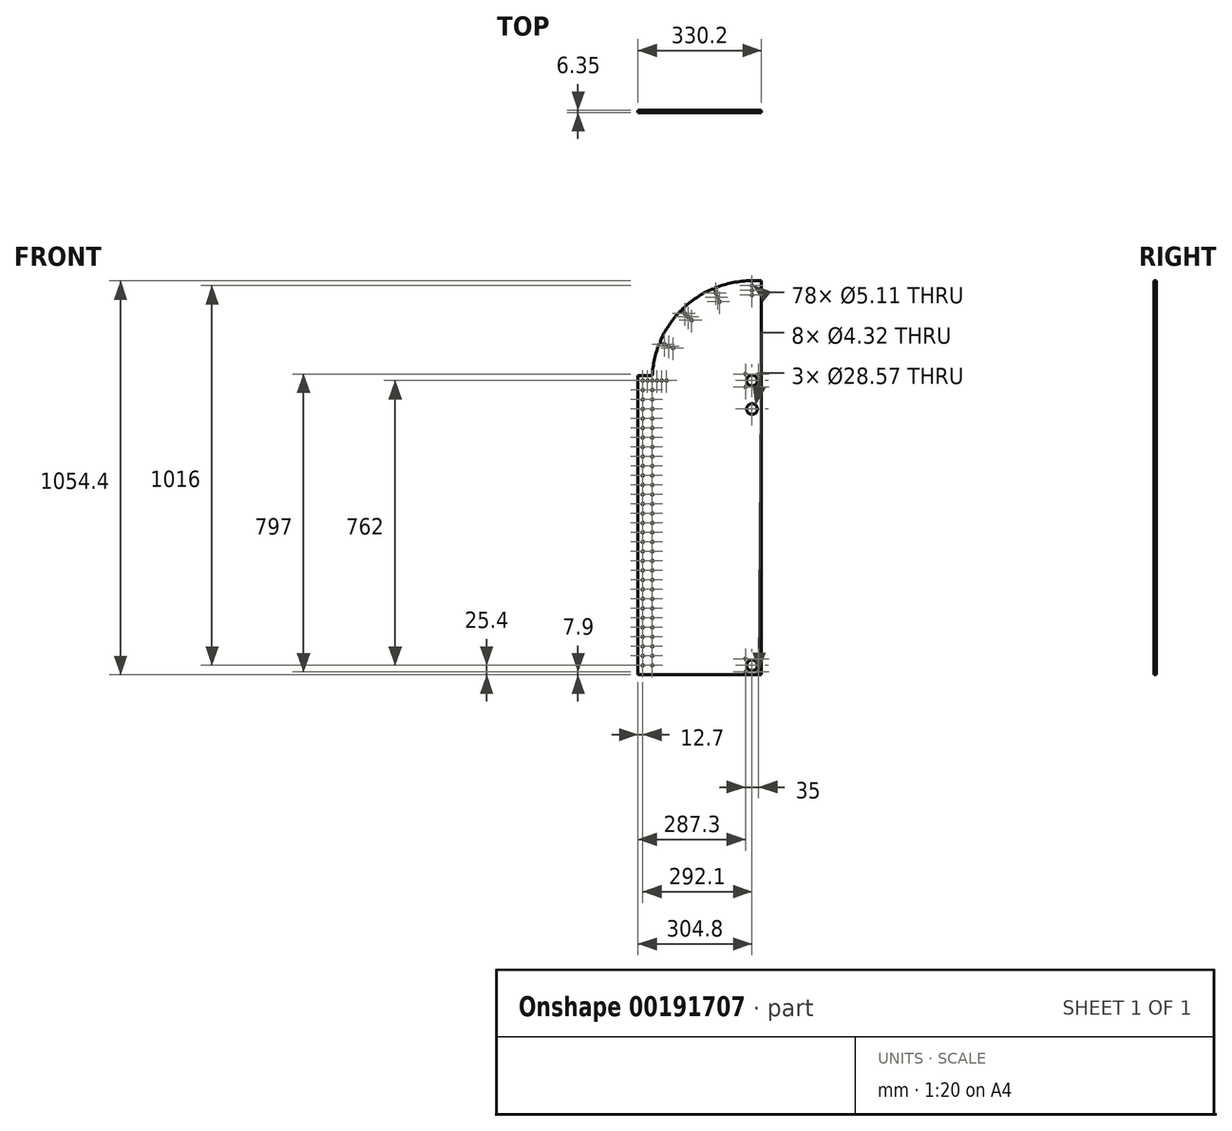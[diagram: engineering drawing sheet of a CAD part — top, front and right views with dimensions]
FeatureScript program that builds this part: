
annotation { "Feature Type Name" : "Feature", "Feature Type Description" : "" }
export const myFeature = defineFeature(function(context is Context, id is Id, definition is map)
    precondition{}
    {
        {
            var Q0;
            Q0=qCreatedBy(makeId("Front.planeOp"),FACE);
            var sketch = newSketch(context, id + "F0", { "sketchPlane" : qUnion([Q0])});
            skCircle(sketch, "E0", {"center": v(0, 0) * mm, "radius": 50.8 * mm, "construction": true});
            skCircle(sketch, "E1", {"center": v(0, 0) * mm, "radius": 14.29 * mm});
            skLineSegment(sketch, "E2", {"start": v(25.4, 0) * mm, "end": v(25.4, -787.4) * mm});
            skCircle(sketch, "E3", {"center": v(0, -76.2) * mm, "radius": 14.29 * mm});
            skLineSegment(sketch, "E4", {"start": v(0, 0) * mm, "end": v(0, -787.4) * mm, "construction": true});
            skCircle(sketch, "E5", {"center": v(0, -76.2) * mm, "radius": 19.05 * mm, "construction": true});
            skCircle(sketch, "E6", {"center": v(0, -762) * mm, "radius": 14.29 * mm});
            skLineSegment(sketch, "E7", {"start": v(25.4, -787.4) * mm, "end": v(-304.8, -787.4) * mm});
            skLineSegment(sketch, "E8", {"start": v(-304.8, -787.4) * mm, "end": v(-304.8, 0) * mm});
            skLineSegment(sketch, "E9", {"start": v(-304.8, 0) * mm, "end": v(-304.8, 304.8) * mm});
            skLineSegment(sketch, "E10", {"start": v(-304.8, 304.8) * mm, "end": v(25.4, 304.8) * mm});
            skLineSegment(sketch, "E11", {"start": v(25.4, 304.8) * mm, "end": v(25.4, 0) * mm});
            skSolve(sketch);
        }
        {
            var Q0;
            Q0 = qSketchRegion(id + "F0", true);
            extrude(context, id + "F1", {"entities" : qUnion([Q0]), "depth" : 6.35 * mm});
        }
        {
            var Q0;
            Q0=makeQuery(id+"F1.opExtrude","CAP_FACE",FACE,{"disambiguationData":[OSD([sQuery(id+"F0.wireOp",EDGE,"E1"),sQuery(id+"F0.wireOp",EDGE,"E2"),sQuery(id+"F0.wireOp",EDGE,"E3"),sQuery(id+"F0.wireOp",EDGE,"E6"),sQuery(id+"F0.wireOp",EDGE,"E7"),sQuery(id+"F0.wireOp",EDGE,"E8"),sQuery(id+"F0.wireOp",EDGE,"E9"),sQuery(id+"F0.wireOp",EDGE,"E10"),sQuery(id+"F0.wireOp",EDGE,"E11")])],"isStart":false});
            var sketch = newSketch(context, id + "F2", { "sketchPlane" : qUnion([Q0])});
            skLineSegment(sketch, "E12", {"start": v(25.4, 0) * mm, "end": v(-304.8, 0) * mm, "construction": true});
            skCircle(sketch, "E13", {"center": v(-292.1, 0) * mm, "radius": 2.55 * mm});
            skCircle(sketch, "E14.0.1.0", {"center": v(-292.1, -25.4) * mm, "radius": 2.55 * mm});
            skCircle(sketch, "E14.0.2.0", {"center": v(-292.1, -50.8) * mm, "radius": 2.55 * mm});
            skCircle(sketch, "E14.0.3.0", {"center": v(-292.1, -76.2) * mm, "radius": 2.55 * mm});
            skCircle(sketch, "E14.0.4.0", {"center": v(-292.1, -101.6) * mm, "radius": 2.55 * mm});
            skCircle(sketch, "E14.0.5.0", {"center": v(-292.1, -127) * mm, "radius": 2.55 * mm});
            skCircle(sketch, "E14.0.6.0", {"center": v(-292.1, -152.4) * mm, "radius": 2.55 * mm});
            skCircle(sketch, "E14.0.7.0", {"center": v(-292.1, -177.8) * mm, "radius": 2.55 * mm});
            skCircle(sketch, "E14.0.8.0", {"center": v(-292.1, -203.2) * mm, "radius": 2.55 * mm});
            skCircle(sketch, "E14.0.9.0", {"center": v(-292.1, -228.6) * mm, "radius": 2.55 * mm});
            skCircle(sketch, "E14.0.10.0", {"center": v(-292.1, -254) * mm, "radius": 2.55 * mm});
            skCircle(sketch, "E14.0.11.0", {"center": v(-292.1, -279.4) * mm, "radius": 2.55 * mm});
            skCircle(sketch, "E14.0.12.0", {"center": v(-292.1, -304.8) * mm, "radius": 2.55 * mm});
            skCircle(sketch, "E14.0.13.0", {"center": v(-292.1, -330.2) * mm, "radius": 2.55 * mm});
            skCircle(sketch, "E14.0.14.0", {"center": v(-292.1, -355.6) * mm, "radius": 2.55 * mm});
            skCircle(sketch, "E14.0.15.0", {"center": v(-292.1, -381) * mm, "radius": 2.55 * mm});
            skCircle(sketch, "E14.0.16.0", {"center": v(-292.1, -406.4) * mm, "radius": 2.55 * mm});
            skCircle(sketch, "E14.0.17.0", {"center": v(-292.1, -431.8) * mm, "radius": 2.55 * mm});
            skCircle(sketch, "E14.0.18.0", {"center": v(-292.1, -457.2) * mm, "radius": 2.55 * mm});
            skCircle(sketch, "E14.0.19.0", {"center": v(-292.1, -482.6) * mm, "radius": 2.55 * mm});
            skCircle(sketch, "E14.0.20.0", {"center": v(-292.1, -508) * mm, "radius": 2.55 * mm});
            skCircle(sketch, "E14.0.21.0", {"center": v(-292.1, -533.4) * mm, "radius": 2.55 * mm});
            skCircle(sketch, "E14.0.22.0", {"center": v(-292.1, -558.8) * mm, "radius": 2.55 * mm});
            skCircle(sketch, "E14.0.23.0", {"center": v(-292.1, -584.2) * mm, "radius": 2.55 * mm});
            skCircle(sketch, "E14.0.24.0", {"center": v(-292.1, -609.6) * mm, "radius": 2.55 * mm});
            skCircle(sketch, "E14.0.25.0", {"center": v(-292.1, -635) * mm, "radius": 2.55 * mm});
            skCircle(sketch, "E14.0.26.0", {"center": v(-292.1, -660.4) * mm, "radius": 2.55 * mm});
            skCircle(sketch, "E14.0.27.0", {"center": v(-292.1, -685.8) * mm, "radius": 2.55 * mm});
            skCircle(sketch, "E14.0.28.0", {"center": v(-292.1, -711.2) * mm, "radius": 2.55 * mm});
            skCircle(sketch, "E14.0.29.0", {"center": v(-292.1, -736.6) * mm, "radius": 2.55 * mm});
            skCircle(sketch, "E14.0.30.0", {"center": v(-292.1, -762) * mm, "radius": 2.55 * mm});
            skCircle(sketch, "E14.1.0.0", {"center": v(-266.7, 0) * mm, "radius": 2.55 * mm});
            skCircle(sketch, "E14.1.1.0", {"center": v(-266.7, -25.4) * mm, "radius": 2.55 * mm});
            skCircle(sketch, "E14.1.2.0", {"center": v(-266.7, -50.8) * mm, "radius": 2.55 * mm});
            skCircle(sketch, "E14.1.3.0", {"center": v(-266.7, -76.2) * mm, "radius": 2.55 * mm});
            skCircle(sketch, "E14.1.4.0", {"center": v(-266.7, -101.6) * mm, "radius": 2.55 * mm});
            skCircle(sketch, "E14.1.5.0", {"center": v(-266.7, -127) * mm, "radius": 2.55 * mm});
            skCircle(sketch, "E14.1.6.0", {"center": v(-266.7, -152.4) * mm, "radius": 2.55 * mm});
            skCircle(sketch, "E14.1.7.0", {"center": v(-266.7, -177.8) * mm, "radius": 2.55 * mm});
            skCircle(sketch, "E14.1.8.0", {"center": v(-266.7, -203.2) * mm, "radius": 2.55 * mm});
            skCircle(sketch, "E14.1.9.0", {"center": v(-266.7, -228.6) * mm, "radius": 2.55 * mm});
            skCircle(sketch, "E14.1.10.0", {"center": v(-266.7, -254) * mm, "radius": 2.55 * mm});
            skCircle(sketch, "E14.1.11.0", {"center": v(-266.7, -279.4) * mm, "radius": 2.55 * mm});
            skCircle(sketch, "E14.1.12.0", {"center": v(-266.7, -304.8) * mm, "radius": 2.55 * mm});
            skCircle(sketch, "E14.1.13.0", {"center": v(-266.7, -330.2) * mm, "radius": 2.55 * mm});
            skCircle(sketch, "E14.1.14.0", {"center": v(-266.7, -355.6) * mm, "radius": 2.55 * mm});
            skCircle(sketch, "E14.1.15.0", {"center": v(-266.7, -381) * mm, "radius": 2.55 * mm});
            skCircle(sketch, "E14.1.16.0", {"center": v(-266.7, -406.4) * mm, "radius": 2.55 * mm});
            skCircle(sketch, "E14.1.17.0", {"center": v(-266.7, -431.8) * mm, "radius": 2.55 * mm});
            skCircle(sketch, "E14.1.18.0", {"center": v(-266.7, -457.2) * mm, "radius": 2.55 * mm});
            skCircle(sketch, "E14.1.19.0", {"center": v(-266.7, -482.6) * mm, "radius": 2.55 * mm});
            skCircle(sketch, "E14.1.20.0", {"center": v(-266.7, -508) * mm, "radius": 2.55 * mm});
            skCircle(sketch, "E14.1.21.0", {"center": v(-266.7, -533.4) * mm, "radius": 2.55 * mm});
            skCircle(sketch, "E14.1.22.0", {"center": v(-266.7, -558.8) * mm, "radius": 2.55 * mm});
            skCircle(sketch, "E14.1.23.0", {"center": v(-266.7, -584.2) * mm, "radius": 2.55 * mm});
            skCircle(sketch, "E14.1.24.0", {"center": v(-266.7, -609.6) * mm, "radius": 2.55 * mm});
            skCircle(sketch, "E14.1.25.0", {"center": v(-266.7, -635) * mm, "radius": 2.55 * mm});
            skCircle(sketch, "E14.1.26.0", {"center": v(-266.7, -660.4) * mm, "radius": 2.55 * mm});
            skCircle(sketch, "E14.1.27.0", {"center": v(-266.7, -685.8) * mm, "radius": 2.55 * mm});
            skCircle(sketch, "E14.1.28.0", {"center": v(-266.7, -711.2) * mm, "radius": 2.55 * mm});
            skCircle(sketch, "E14.1.29.0", {"center": v(-266.7, -736.6) * mm, "radius": 2.55 * mm});
            skCircle(sketch, "E14.1.30.0", {"center": v(-266.7, -762) * mm, "radius": 2.55 * mm});
            skLineSegment(sketch, "E14.direction1", {"start": v(-292.1, 0) * mm, "end": v(-266.7, 0) * mm, "construction": true});
            skLineSegment(sketch, "E14.direction2", {"start": v(-292.1, 0) * mm, "end": v(-292.1, -25.4) * mm, "construction": true});
            skSolve(sketch);
        }
        {
            var Q0;
            Q0=makeQuery(id+"F2.imprint","IMPRINT",FACE,{"disambiguationData":[TD([[makeQuery(id+"F2.imprint","IMPRINT",EDGE,{"derivedFrom":sQuery(id+"F2.wireOp",EDGE,"E14.0.1.0")}),1.0]])]});
            var Q1;
            Q1=makeQuery(id+"F2.imprint","IMPRINT",FACE,{"disambiguationData":[TD([[makeQuery(id+"F2.imprint","IMPRINT",EDGE,{"derivedFrom":sQuery(id+"F2.wireOp",EDGE,"E14.0.2.0")}),1.0]])]});
            var Q2;
            Q2=makeQuery(id+"F2.imprint","IMPRINT",FACE,{"disambiguationData":[TD([[makeQuery(id+"F2.imprint","IMPRINT",EDGE,{"derivedFrom":sQuery(id+"F2.wireOp",EDGE,"E14.1.2.0")}),1.0]])]});
            var Q3;
            Q3=makeQuery(id+"F2.imprint","IMPRINT",FACE,{"disambiguationData":[TD([[makeQuery(id+"F2.imprint","IMPRINT",EDGE,{"derivedFrom":sQuery(id+"F2.wireOp",EDGE,"E14.1.1.0")}),1.0]])]});
            var Q4;
            Q4=makeQuery(id+"F2.imprint","IMPRINT",FACE,{"disambiguationData":[TD([[makeQuery(id+"F2.imprint","IMPRINT",EDGE,{"derivedFrom":sQuery(id+"F2.wireOp",EDGE,"E14.1.0.0")}),1.0]])]});
            var Q5;
            Q5=makeQuery(id+"F2.imprint","IMPRINT",FACE,{"disambiguationData":[TD([[makeQuery(id+"F2.imprint","IMPRINT",EDGE,{"derivedFrom":sQuery(id+"F2.wireOp",EDGE,"E13")}),1.0]])]});
            var Q6;
            Q6=makeQuery(id+"F2.imprint","IMPRINT",FACE,{"disambiguationData":[TD([[makeQuery(id+"F2.imprint","IMPRINT",EDGE,{"derivedFrom":sQuery(id+"F2.wireOp",EDGE,"E14.0.3.0")}),1.0]])]});
            var Q7;
            Q7=makeQuery(id+"F2.imprint","IMPRINT",FACE,{"disambiguationData":[TD([[makeQuery(id+"F2.imprint","IMPRINT",EDGE,{"derivedFrom":sQuery(id+"F2.wireOp",EDGE,"E14.1.3.0")}),1.0]])]});
            var Q8;
            Q8=makeQuery(id+"F2.imprint","IMPRINT",FACE,{"disambiguationData":[TD([[makeQuery(id+"F2.imprint","IMPRINT",EDGE,{"derivedFrom":sQuery(id+"F2.wireOp",EDGE,"E14.0.4.0")}),1.0]])]});
            var Q9;
            Q9=makeQuery(id+"F2.imprint","IMPRINT",FACE,{"disambiguationData":[TD([[makeQuery(id+"F2.imprint","IMPRINT",EDGE,{"derivedFrom":sQuery(id+"F2.wireOp",EDGE,"E14.1.4.0")}),1.0]])]});
            var Q10;
            Q10=makeQuery(id+"F2.imprint","IMPRINT",FACE,{"disambiguationData":[TD([[makeQuery(id+"F2.imprint","IMPRINT",EDGE,{"derivedFrom":sQuery(id+"F2.wireOp",EDGE,"E14.1.5.0")}),1.0]])]});
            var Q11;
            Q11=makeQuery(id+"F2.imprint","IMPRINT",FACE,{"disambiguationData":[TD([[makeQuery(id+"F2.imprint","IMPRINT",EDGE,{"derivedFrom":sQuery(id+"F2.wireOp",EDGE,"E14.0.5.0")}),1.0]])]});
            var Q12;
            Q12=makeQuery(id+"F2.imprint","IMPRINT",FACE,{"disambiguationData":[TD([[makeQuery(id+"F2.imprint","IMPRINT",EDGE,{"derivedFrom":sQuery(id+"F2.wireOp",EDGE,"E14.0.6.0")}),1.0]])]});
            var Q13;
            Q13=makeQuery(id+"F2.imprint","IMPRINT",FACE,{"disambiguationData":[TD([[makeQuery(id+"F2.imprint","IMPRINT",EDGE,{"derivedFrom":sQuery(id+"F2.wireOp",EDGE,"E14.1.6.0")}),1.0]])]});
            var Q14;
            Q14=makeQuery(id+"F2.imprint","IMPRINT",FACE,{"disambiguationData":[TD([[makeQuery(id+"F2.imprint","IMPRINT",EDGE,{"derivedFrom":sQuery(id+"F2.wireOp",EDGE,"E14.0.7.0")}),1.0]])]});
            var Q15;
            Q15=makeQuery(id+"F2.imprint","IMPRINT",FACE,{"disambiguationData":[TD([[makeQuery(id+"F2.imprint","IMPRINT",EDGE,{"derivedFrom":sQuery(id+"F2.wireOp",EDGE,"E14.1.7.0")}),1.0]])]});
            var Q16;
            Q16=makeQuery(id+"F2.imprint","IMPRINT",FACE,{"disambiguationData":[TD([[makeQuery(id+"F2.imprint","IMPRINT",EDGE,{"derivedFrom":sQuery(id+"F2.wireOp",EDGE,"E14.1.8.0")}),1.0]])]});
            var Q17;
            Q17=makeQuery(id+"F2.imprint","IMPRINT",FACE,{"disambiguationData":[TD([[makeQuery(id+"F2.imprint","IMPRINT",EDGE,{"derivedFrom":sQuery(id+"F2.wireOp",EDGE,"E14.0.8.0")}),1.0]])]});
            var Q18;
            Q18=makeQuery(id+"F2.imprint","IMPRINT",FACE,{"disambiguationData":[TD([[makeQuery(id+"F2.imprint","IMPRINT",EDGE,{"derivedFrom":sQuery(id+"F2.wireOp",EDGE,"E14.0.9.0")}),1.0]])]});
            var Q19;
            Q19=makeQuery(id+"F2.imprint","IMPRINT",FACE,{"disambiguationData":[TD([[makeQuery(id+"F2.imprint","IMPRINT",EDGE,{"derivedFrom":sQuery(id+"F2.wireOp",EDGE,"E14.1.9.0")}),1.0]])]});
            var Q20;
            Q20=makeQuery(id+"F2.imprint","IMPRINT",FACE,{"disambiguationData":[TD([[makeQuery(id+"F2.imprint","IMPRINT",EDGE,{"derivedFrom":sQuery(id+"F2.wireOp",EDGE,"E14.0.10.0")}),1.0]])]});
            var Q21;
            Q21=makeQuery(id+"F2.imprint","IMPRINT",FACE,{"disambiguationData":[TD([[makeQuery(id+"F2.imprint","IMPRINT",EDGE,{"derivedFrom":sQuery(id+"F2.wireOp",EDGE,"E14.1.10.0")}),1.0]])]});
            var Q22;
            Q22=makeQuery(id+"F2.imprint","IMPRINT",FACE,{"disambiguationData":[TD([[makeQuery(id+"F2.imprint","IMPRINT",EDGE,{"derivedFrom":sQuery(id+"F2.wireOp",EDGE,"E14.1.11.0")}),1.0]])]});
            var Q23;
            Q23=makeQuery(id+"F2.imprint","IMPRINT",FACE,{"disambiguationData":[TD([[makeQuery(id+"F2.imprint","IMPRINT",EDGE,{"derivedFrom":sQuery(id+"F2.wireOp",EDGE,"E14.0.11.0")}),1.0]])]});
            var Q24;
            Q24=makeQuery(id+"F2.imprint","IMPRINT",FACE,{"disambiguationData":[TD([[makeQuery(id+"F2.imprint","IMPRINT",EDGE,{"derivedFrom":sQuery(id+"F2.wireOp",EDGE,"E14.0.12.0")}),1.0]])]});
            var Q25;
            Q25=makeQuery(id+"F2.imprint","IMPRINT",FACE,{"disambiguationData":[TD([[makeQuery(id+"F2.imprint","IMPRINT",EDGE,{"derivedFrom":sQuery(id+"F2.wireOp",EDGE,"E14.1.12.0")}),1.0]])]});
            var Q26;
            Q26=makeQuery(id+"F2.imprint","IMPRINT",FACE,{"disambiguationData":[TD([[makeQuery(id+"F2.imprint","IMPRINT",EDGE,{"derivedFrom":sQuery(id+"F2.wireOp",EDGE,"E14.1.13.0")}),1.0]])]});
            var Q27;
            Q27=makeQuery(id+"F2.imprint","IMPRINT",FACE,{"disambiguationData":[TD([[makeQuery(id+"F2.imprint","IMPRINT",EDGE,{"derivedFrom":sQuery(id+"F2.wireOp",EDGE,"E14.0.13.0")}),1.0]])]});
            var Q28;
            Q28=makeQuery(id+"F2.imprint","IMPRINT",FACE,{"disambiguationData":[TD([[makeQuery(id+"F2.imprint","IMPRINT",EDGE,{"derivedFrom":sQuery(id+"F2.wireOp",EDGE,"E14.0.14.0")}),1.0]])]});
            var Q29;
            Q29=makeQuery(id+"F2.imprint","IMPRINT",FACE,{"disambiguationData":[TD([[makeQuery(id+"F2.imprint","IMPRINT",EDGE,{"derivedFrom":sQuery(id+"F2.wireOp",EDGE,"E14.1.14.0")}),1.0]])]});
            var Q30;
            Q30=makeQuery(id+"F2.imprint","IMPRINT",FACE,{"disambiguationData":[TD([[makeQuery(id+"F2.imprint","IMPRINT",EDGE,{"derivedFrom":sQuery(id+"F2.wireOp",EDGE,"E14.1.15.0")}),1.0]])]});
            var Q31;
            Q31=makeQuery(id+"F2.imprint","IMPRINT",FACE,{"disambiguationData":[TD([[makeQuery(id+"F2.imprint","IMPRINT",EDGE,{"derivedFrom":sQuery(id+"F2.wireOp",EDGE,"E14.0.15.0")}),1.0]])]});
            var Q32;
            Q32=makeQuery(id+"F2.imprint","IMPRINT",FACE,{"disambiguationData":[TD([[makeQuery(id+"F2.imprint","IMPRINT",EDGE,{"derivedFrom":sQuery(id+"F2.wireOp",EDGE,"E14.1.16.0")}),1.0]])]});
            var Q33;
            Q33=makeQuery(id+"F2.imprint","IMPRINT",FACE,{"disambiguationData":[TD([[makeQuery(id+"F2.imprint","IMPRINT",EDGE,{"derivedFrom":sQuery(id+"F2.wireOp",EDGE,"E14.0.16.0")}),1.0]])]});
            var Q34;
            Q34=makeQuery(id+"F2.imprint","IMPRINT",FACE,{"disambiguationData":[TD([[makeQuery(id+"F2.imprint","IMPRINT",EDGE,{"derivedFrom":sQuery(id+"F2.wireOp",EDGE,"E14.0.17.0")}),1.0]])]});
            var Q35;
            Q35=makeQuery(id+"F2.imprint","IMPRINT",FACE,{"disambiguationData":[TD([[makeQuery(id+"F2.imprint","IMPRINT",EDGE,{"derivedFrom":sQuery(id+"F2.wireOp",EDGE,"E14.1.17.0")}),1.0]])]});
            var Q36;
            Q36=makeQuery(id+"F2.imprint","IMPRINT",FACE,{"disambiguationData":[TD([[makeQuery(id+"F2.imprint","IMPRINT",EDGE,{"derivedFrom":sQuery(id+"F2.wireOp",EDGE,"E14.1.18.0")}),1.0]])]});
            var Q37;
            Q37=makeQuery(id+"F2.imprint","IMPRINT",FACE,{"disambiguationData":[TD([[makeQuery(id+"F2.imprint","IMPRINT",EDGE,{"derivedFrom":sQuery(id+"F2.wireOp",EDGE,"E14.0.18.0")}),1.0]])]});
            var Q38;
            Q38=makeQuery(id+"F2.imprint","IMPRINT",FACE,{"disambiguationData":[TD([[makeQuery(id+"F2.imprint","IMPRINT",EDGE,{"derivedFrom":sQuery(id+"F2.wireOp",EDGE,"E14.1.19.0")}),1.0]])]});
            var Q39;
            Q39=makeQuery(id+"F2.imprint","IMPRINT",FACE,{"disambiguationData":[TD([[makeQuery(id+"F2.imprint","IMPRINT",EDGE,{"derivedFrom":sQuery(id+"F2.wireOp",EDGE,"E14.0.19.0")}),1.0]])]});
            var Q40;
            Q40=makeQuery(id+"F2.imprint","IMPRINT",FACE,{"disambiguationData":[TD([[makeQuery(id+"F2.imprint","IMPRINT",EDGE,{"derivedFrom":sQuery(id+"F2.wireOp",EDGE,"E14.0.20.0")}),1.0]])]});
            var Q41;
            Q41=makeQuery(id+"F2.imprint","IMPRINT",FACE,{"disambiguationData":[TD([[makeQuery(id+"F2.imprint","IMPRINT",EDGE,{"derivedFrom":sQuery(id+"F2.wireOp",EDGE,"E14.1.20.0")}),1.0]])]});
            var Q42;
            Q42=makeQuery(id+"F2.imprint","IMPRINT",FACE,{"disambiguationData":[TD([[makeQuery(id+"F2.imprint","IMPRINT",EDGE,{"derivedFrom":sQuery(id+"F2.wireOp",EDGE,"E14.1.21.0")}),1.0]])]});
            var Q43;
            Q43=makeQuery(id+"F2.imprint","IMPRINT",FACE,{"disambiguationData":[TD([[makeQuery(id+"F2.imprint","IMPRINT",EDGE,{"derivedFrom":sQuery(id+"F2.wireOp",EDGE,"E14.0.21.0")}),1.0]])]});
            var Q44;
            Q44=makeQuery(id+"F2.imprint","IMPRINT",FACE,{"disambiguationData":[TD([[makeQuery(id+"F2.imprint","IMPRINT",EDGE,{"derivedFrom":sQuery(id+"F2.wireOp",EDGE,"E14.1.22.0")}),1.0]])]});
            var Q45;
            Q45=makeQuery(id+"F2.imprint","IMPRINT",FACE,{"disambiguationData":[TD([[makeQuery(id+"F2.imprint","IMPRINT",EDGE,{"derivedFrom":sQuery(id+"F2.wireOp",EDGE,"E14.0.22.0")}),1.0]])]});
            var Q46;
            Q46=makeQuery(id+"F2.imprint","IMPRINT",FACE,{"disambiguationData":[TD([[makeQuery(id+"F2.imprint","IMPRINT",EDGE,{"derivedFrom":sQuery(id+"F2.wireOp",EDGE,"E14.0.23.0")}),1.0]])]});
            var Q47;
            Q47=makeQuery(id+"F2.imprint","IMPRINT",FACE,{"disambiguationData":[TD([[makeQuery(id+"F2.imprint","IMPRINT",EDGE,{"derivedFrom":sQuery(id+"F2.wireOp",EDGE,"E14.1.23.0")}),1.0]])]});
            var Q48;
            Q48=makeQuery(id+"F2.imprint","IMPRINT",FACE,{"disambiguationData":[TD([[makeQuery(id+"F2.imprint","IMPRINT",EDGE,{"derivedFrom":sQuery(id+"F2.wireOp",EDGE,"E14.1.24.0")}),1.0]])]});
            var Q49;
            Q49=makeQuery(id+"F2.imprint","IMPRINT",FACE,{"disambiguationData":[TD([[makeQuery(id+"F2.imprint","IMPRINT",EDGE,{"derivedFrom":sQuery(id+"F2.wireOp",EDGE,"E14.0.24.0")}),1.0]])]});
            var Q50;
            Q50=makeQuery(id+"F2.imprint","IMPRINT",FACE,{"disambiguationData":[TD([[makeQuery(id+"F2.imprint","IMPRINT",EDGE,{"derivedFrom":sQuery(id+"F2.wireOp",EDGE,"E14.1.25.0")}),1.0]])]});
            var Q51;
            Q51=makeQuery(id+"F2.imprint","IMPRINT",FACE,{"disambiguationData":[TD([[makeQuery(id+"F2.imprint","IMPRINT",EDGE,{"derivedFrom":sQuery(id+"F2.wireOp",EDGE,"E14.0.25.0")}),1.0]])]});
            var Q52;
            Q52=makeQuery(id+"F2.imprint","IMPRINT",FACE,{"disambiguationData":[TD([[makeQuery(id+"F2.imprint","IMPRINT",EDGE,{"derivedFrom":sQuery(id+"F2.wireOp",EDGE,"E14.0.26.0")}),1.0]])]});
            var Q53;
            Q53=makeQuery(id+"F2.imprint","IMPRINT",FACE,{"disambiguationData":[TD([[makeQuery(id+"F2.imprint","IMPRINT",EDGE,{"derivedFrom":sQuery(id+"F2.wireOp",EDGE,"E14.1.26.0")}),1.0]])]});
            var Q54;
            Q54=makeQuery(id+"F2.imprint","IMPRINT",FACE,{"disambiguationData":[TD([[makeQuery(id+"F2.imprint","IMPRINT",EDGE,{"derivedFrom":sQuery(id+"F2.wireOp",EDGE,"E14.1.27.0")}),1.0]])]});
            var Q55;
            Q55=makeQuery(id+"F2.imprint","IMPRINT",FACE,{"disambiguationData":[TD([[makeQuery(id+"F2.imprint","IMPRINT",EDGE,{"derivedFrom":sQuery(id+"F2.wireOp",EDGE,"E14.0.27.0")}),1.0]])]});
            var Q56;
            Q56=makeQuery(id+"F2.imprint","IMPRINT",FACE,{"disambiguationData":[TD([[makeQuery(id+"F2.imprint","IMPRINT",EDGE,{"derivedFrom":sQuery(id+"F2.wireOp",EDGE,"E14.1.28.0")}),1.0]])]});
            var Q57;
            Q57=makeQuery(id+"F2.imprint","IMPRINT",FACE,{"disambiguationData":[TD([[makeQuery(id+"F2.imprint","IMPRINT",EDGE,{"derivedFrom":sQuery(id+"F2.wireOp",EDGE,"E14.0.28.0")}),1.0]])]});
            var Q58;
            Q58=makeQuery(id+"F2.imprint","IMPRINT",FACE,{"disambiguationData":[TD([[makeQuery(id+"F2.imprint","IMPRINT",EDGE,{"derivedFrom":sQuery(id+"F2.wireOp",EDGE,"E14.0.29.0")}),1.0]])]});
            var Q59;
            Q59=makeQuery(id+"F2.imprint","IMPRINT",FACE,{"disambiguationData":[TD([[makeQuery(id+"F2.imprint","IMPRINT",EDGE,{"derivedFrom":sQuery(id+"F2.wireOp",EDGE,"E14.1.29.0")}),1.0]])]});
            var Q60;
            Q60=makeQuery(id+"F2.imprint","IMPRINT",FACE,{"disambiguationData":[TD([[makeQuery(id+"F2.imprint","IMPRINT",EDGE,{"derivedFrom":sQuery(id+"F2.wireOp",EDGE,"E14.1.30.0")}),1.0]])]});
            var Q61;
            Q61=makeQuery(id+"F2.imprint","IMPRINT",FACE,{"disambiguationData":[TD([[makeQuery(id+"F2.imprint","IMPRINT",EDGE,{"derivedFrom":sQuery(id+"F2.wireOp",EDGE,"E14.0.30.0")}),1.0]])]});
            var Q62;
            Q62=makeQuery(id+"F2.imprint","IMPRINT",FACE,{"disambiguationData":[TD([[makeQuery(id+"F2.imprint","IMPRINT",EDGE,{"derivedFrom":sQuery(id+"F2.wireOp",EDGE,"E14.0.31.0")}),1.0]])]});
            var Q63;
            Q63=makeQuery(id+"F2.imprint","IMPRINT",FACE,{"disambiguationData":[TD([[makeQuery(id+"F2.imprint","IMPRINT",EDGE,{"derivedFrom":sQuery(id+"F2.wireOp",EDGE,"E14.1.31.0")}),1.0]])]});
            extrude(context, id + "F3", {"entities" : qUnion([Q0, Q1, Q2, Q3, Q4, Q5, Q6, Q7, Q8, Q9, Q10, Q11, Q12, Q13, Q14, Q15, Q16, Q17, Q18, Q19, Q20, Q21, Q22, Q23, Q24, Q25, Q26, Q27, Q28, Q29, Q30, Q31, Q32, Q33, Q34, Q35, Q36, Q37, Q38, Q39, Q40, Q41, Q42, Q43, Q44, Q45, Q46, Q47, Q48, Q49, Q50, Q51, Q52, Q53, Q54, Q55, Q56, Q57, Q58, Q59, Q60, Q61, Q62, Q63]), "operationType" : NewBodyOperationType.REMOVE, "oppositeDirection" : true, "depth" : 25.4 * mm});
        }
        {
            var Q0;
            Q0=makeQuery(id+"F1.opExtrude","CAP_FACE",FACE,{"disambiguationData":[OSD([sQuery(id+"F0.wireOp",EDGE,"E1"),sQuery(id+"F0.wireOp",EDGE,"E2"),sQuery(id+"F0.wireOp",EDGE,"E3"),sQuery(id+"F0.wireOp",EDGE,"E6"),sQuery(id+"F0.wireOp",EDGE,"E7"),sQuery(id+"F0.wireOp",EDGE,"E8"),sQuery(id+"F0.wireOp",EDGE,"E9"),sQuery(id+"F0.wireOp",EDGE,"E10"),sQuery(id+"F0.wireOp",EDGE,"E11")])],"isStart":false});
            var sketch = newSketch(context, id + "F4", { "sketchPlane" : qUnion([Q0])});
            skLineSegment(sketch, "E15.bottom", {"start": v(17.5, 17.5) * mm, "end": v(-17.5, 17.5) * mm, "construction": true});
            skLineSegment(sketch, "E15.top", {"start": v(17.5, -17.5) * mm, "end": v(-17.5, -17.5) * mm, "construction": true});
            skLineSegment(sketch, "E15.left", {"start": v(17.5, 17.5) * mm, "end": v(17.5, -17.5) * mm, "construction": true});
            skLineSegment(sketch, "E15.right", {"start": v(-17.5, 17.5) * mm, "end": v(-17.5, -17.5) * mm, "construction": true});
            skPoint(sketch, "E15.middle", {"position": v(0, 0) * mm});
            skLineSegment(sketch, "E16.bottom", {"start": v(17.5, -744.5) * mm, "end": v(-17.5, -744.5) * mm, "construction": true});
            skLineSegment(sketch, "E16.top", {"start": v(17.5, -779.5) * mm, "end": v(-17.5, -779.5) * mm, "construction": true});
            skLineSegment(sketch, "E16.left", {"start": v(17.5, -744.5) * mm, "end": v(17.5, -779.5) * mm, "construction": true});
            skLineSegment(sketch, "E16.right", {"start": v(-17.5, -744.5) * mm, "end": v(-17.5, -779.5) * mm, "construction": true});
            skPoint(sketch, "E16.middle", {"position": v(0, -762) * mm});
            skCircle(sketch, "E17", {"center": v(-17.5, -744.5) * mm, "radius": 2.16 * mm});
            skCircle(sketch, "E18", {"center": v(17.5, -744.5) * mm, "radius": 2.16 * mm});
            skCircle(sketch, "E19", {"center": v(17.5, -779.5) * mm, "radius": 2.16 * mm});
            skCircle(sketch, "E20", {"center": v(-17.5, -779.5) * mm, "radius": 2.16 * mm});
            skCircle(sketch, "E21", {"center": v(17.5, -17.5) * mm, "radius": 2.16 * mm});
            skCircle(sketch, "E22", {"center": v(17.5, 17.5) * mm, "radius": 2.16 * mm});
            skCircle(sketch, "E23", {"center": v(-17.5, 17.5) * mm, "radius": 2.16 * mm});
            skCircle(sketch, "E24", {"center": v(-17.5, -17.5) * mm, "radius": 2.16 * mm});
            skSolve(sketch);
        }
        {
            var Q0;
            Q0 = qSketchRegion(id + "F4", true);
            extrude(context, id + "F5", {"entities" : qUnion([Q0]), "operationType" : NewBodyOperationType.REMOVE, "oppositeDirection" : true, "depth" : 25.4 * mm});
        }
        {
            var Q0;
            Q0=makeQuery(id+"F1.opExtrude","CAP_FACE",FACE,{"disambiguationData":[OSD([sQuery(id+"F0.wireOp",EDGE,"E1"),sQuery(id+"F0.wireOp",EDGE,"E2"),sQuery(id+"F0.wireOp",EDGE,"E3"),sQuery(id+"F0.wireOp",EDGE,"E6"),sQuery(id+"F0.wireOp",EDGE,"E7"),sQuery(id+"F0.wireOp",EDGE,"E8"),sQuery(id+"F0.wireOp",EDGE,"E9"),sQuery(id+"F0.wireOp",EDGE,"E10"),sQuery(id+"F0.wireOp",EDGE,"E11")])],"isStart":false});
            var sketch = newSketch(context, id + "F6", { "sketchPlane" : qUnion([Q0])});
            skLineSegment(sketch, "E25", {"start": v(0, 0) * mm, "end": v(-254, 0) * mm, "construction": true});
            skCircle(sketch, "E26", {"center": v(-254, 0) * mm, "radius": 2.55 * mm});
            skCircle(sketch, "E27", {"center": v(-266.7, 0) * mm, "radius": 2.55 * mm});
            skCircle(sketch, "E28", {"center": v(-279.4, 0) * mm, "radius": 2.55 * mm});
            skCircle(sketch, "E29", {"center": v(-241.3, 0) * mm, "radius": 2.55 * mm});
            skCircle(sketch, "E30", {"center": v(-228.6, 0) * mm, "radius": 2.55 * mm});
            skCircle(sketch, "E31.1.0", {"center": v(-211.2, 87.48) * mm, "radius": 2.55 * mm});
            skCircle(sketch, "E31.1.1", {"center": v(-222.93, 92.34) * mm, "radius": 2.55 * mm});
            skCircle(sketch, "E31.1.2", {"center": v(-234.67, 97.2) * mm, "radius": 2.55 * mm});
            skCircle(sketch, "E31.1.3", {"center": v(-246.4, 102.06) * mm, "radius": 2.55 * mm});
            skCircle(sketch, "E31.1.4", {"center": v(-258.13, 106.92) * mm, "radius": 2.55 * mm});
            skCircle(sketch, "E31.2.0", {"center": v(-161.64, 161.64) * mm, "radius": 2.55 * mm});
            skCircle(sketch, "E31.2.1", {"center": v(-170.62, 170.62) * mm, "radius": 2.55 * mm});
            skCircle(sketch, "E31.2.2", {"center": v(-179.6, 179.6) * mm, "radius": 2.55 * mm});
            skCircle(sketch, "E31.2.3", {"center": v(-188.59, 188.59) * mm, "radius": 2.55 * mm});
            skCircle(sketch, "E31.2.4", {"center": v(-197.57, 197.57) * mm, "radius": 2.55 * mm});
            skCircle(sketch, "E31.3.0", {"center": v(-87.48, 211.2) * mm, "radius": 2.55 * mm});
            skCircle(sketch, "E31.3.1", {"center": v(-92.34, 222.93) * mm, "radius": 2.55 * mm});
            skCircle(sketch, "E31.3.2", {"center": v(-97.2, 234.67) * mm, "radius": 2.55 * mm});
            skCircle(sketch, "E31.3.3", {"center": v(-102.06, 246.4) * mm, "radius": 2.55 * mm});
            skCircle(sketch, "E31.3.4", {"center": v(-106.92, 258.13) * mm, "radius": 2.55 * mm});
            skCircle(sketch, "E31.4.0", {"center": v(0, 228.6) * mm, "radius": 2.55 * mm});
            skCircle(sketch, "E31.4.1", {"center": v(0, 241.3) * mm, "radius": 2.55 * mm});
            skCircle(sketch, "E31.4.2", {"center": v(0, 254) * mm, "radius": 2.55 * mm});
            skCircle(sketch, "E31.4.3", {"center": v(0, 266.7) * mm, "radius": 2.55 * mm});
            skCircle(sketch, "E31.4.4", {"center": v(0, 279.4) * mm, "radius": 2.55 * mm});
            skPoint(sketch, "E31.center", {"position": v(0, 0) * mm});
            skLineSegment(sketch, "E31.anchor1", {"start": v(0, 0) * mm, "end": v(-279.4, 0) * mm, "construction": true});
            skLineSegment(sketch, "E31.anchor2", {"start": v(0, 0) * mm, "end": v(0, 279.4) * mm, "construction": true});
            skSolve(sketch);
        }
        {
            var Q0;
            Q0=sQuery(id+"F6.wireOp",VERTEX,"E31.3.0.center");
            var Q1;
            Q1=sQuery(id+"F6.wireOp",VERTEX,"E31.3.1.center");
            var Q2;
            Q2=sQuery(id+"F6.wireOp",VERTEX,"E31.3.2.center");
            var Q3;
            Q3=sQuery(id+"F6.wireOp",VERTEX,"E31.3.3.center");
            var Q4;
            Q4=sQuery(id+"F6.wireOp",VERTEX,"E31.3.4.center");
            var Q5;
            Q5=sQuery(id+"F6.wireOp",VERTEX,"E31.4.3.center");
            var Q6;
            Q6=sQuery(id+"F6.wireOp",VERTEX,"E31.4.2.center");
            var Q7;
            Q7=sQuery(id+"F6.wireOp",VERTEX,"E31.4.1.center");
            var Q8;
            Q8=sQuery(id+"F6.wireOp",VERTEX,"E31.4.0.center");
            var Q9;
            Q9=sQuery(id+"F6.wireOp",VERTEX,"E31.anchor2.end");
            var Q10;
            Q10=sQuery(id+"F6.wireOp",VERTEX,"E27.center");
            var Q11;
            Q11=sQuery(id+"F6.wireOp",VERTEX,"E26.center");
            var Q12;
            Q12=sQuery(id+"F6.wireOp",VERTEX,"E31.anchor1.end");
            var Q13;
            Q13=sQuery(id+"F6.wireOp",VERTEX,"E31.1.4.center");
            var Q14;
            Q14=sQuery(id+"F6.wireOp",VERTEX,"E31.1.3.center");
            var Q15;
            Q15=sQuery(id+"F6.wireOp",VERTEX,"E31.1.2.center");
            var Q16;
            Q16=sQuery(id+"F6.wireOp",VERTEX,"E29.center");
            var Q17;
            Q17=sQuery(id+"F6.wireOp",VERTEX,"E30.center");
            var Q18;
            Q18=sQuery(id+"F6.wireOp",VERTEX,"E31.1.1.center");
            var Q19;
            Q19=sQuery(id+"F6.wireOp",VERTEX,"E31.2.0.center");
            var Q20;
            Q20=sQuery(id+"F6.wireOp",VERTEX,"E31.2.1.center");
            var Q21;
            Q21=sQuery(id+"F6.wireOp",VERTEX,"E31.2.3.center");
            var Q22;
            Q22=sQuery(id+"F6.wireOp",VERTEX,"E31.2.2.center");
            var Q23;
            Q23=sQuery(id+"F6.wireOp",VERTEX,"E31.1.0.center");
            var Q24;
            Q24=sQuery(id+"F6.wireOp",VERTEX,"E31.2.4.center");
            var Q25;
            Q25=makeQuery(id+"F1.opExtrude","SWEPT_BODY",BODY,{"disambiguationData":[OSD([sQuery(id+"F0.wireOp",EDGE,"E1"),sQuery(id+"F0.wireOp",EDGE,"E2"),sQuery(id+"F0.wireOp",EDGE,"E3"),sQuery(id+"F0.wireOp",EDGE,"E6"),sQuery(id+"F0.wireOp",EDGE,"E7"),sQuery(id+"F0.wireOp",EDGE,"E8"),sQuery(id+"F0.wireOp",EDGE,"E9"),sQuery(id+"F0.wireOp",EDGE,"E10"),sQuery(id+"F0.wireOp",EDGE,"E11")])]});
            hole(context, id + "F7", {"style" : HoleStyle.SIMPLE, "endStyle" : HoleEndStyle.THROUGH, "holeDiameter" : 5.1 * mm, "tappedDepth" : 12.7 * mm, "tapClearance" : 3, "locations" : qUnion([Q0, Q1, Q2, Q3, Q4, Q5, Q6, Q7, Q8, Q9, Q10, Q11, Q12, Q13, Q14, Q15, Q16, Q17, Q18, Q19, Q20, Q21, Q22, Q23, Q24]), "scope" : qUnion([Q25])});
        }
        {
            var Q0;
            Q0=makeQuery(id+"F1.opExtrude","CAP_FACE",FACE,{"disambiguationData":[OSD([sQuery(id+"F0.wireOp",EDGE,"E1"),sQuery(id+"F0.wireOp",EDGE,"E2"),sQuery(id+"F0.wireOp",EDGE,"E3"),sQuery(id+"F0.wireOp",EDGE,"E6"),sQuery(id+"F0.wireOp",EDGE,"E7"),sQuery(id+"F0.wireOp",EDGE,"E8"),sQuery(id+"F0.wireOp",EDGE,"E9"),sQuery(id+"F0.wireOp",EDGE,"E10"),sQuery(id+"F0.wireOp",EDGE,"E11")])],"isStart":false});
            var sketch = newSketch(context, id + "F8", { "sketchPlane" : qUnion([Q0])});
            skLineSegment(sketch, "E32", {"start": v(-304.8, 12.7) * mm, "end": v(-266.7, 12.7) * mm});
            skArc(sketch, "E33", {"start": v(-266.7, 12.7) * mm, "mid": v(-184.25, 193.24) * mm, "end": v(0, 267) * mm});
            skLineSegment(sketch, "E34", {"start": v(0, 267) * mm, "end": v(25.4, 267) * mm});
            skLineSegment(sketch, "E35", {"start": v(25.4, 267) * mm, "end": v(25.4, 304.8) * mm});
            skLineSegment(sketch, "E36", {"start": v(25.4, 304.8) * mm, "end": v(-304.8, 304.8) * mm});
            skLineSegment(sketch, "E37", {"start": v(-304.8, 304.8) * mm, "end": v(-304.8, 12.7) * mm});
            skSolve(sketch);
        }
        {
            var Q0;
            Q0 = qSketchRegion(id + "F8", true);
            extrude(context, id + "F9", {"entities" : qUnion([Q0]), "operationType" : NewBodyOperationType.REMOVE, "oppositeDirection" : true, "depth" : 25.4 * mm});
        }
    });
